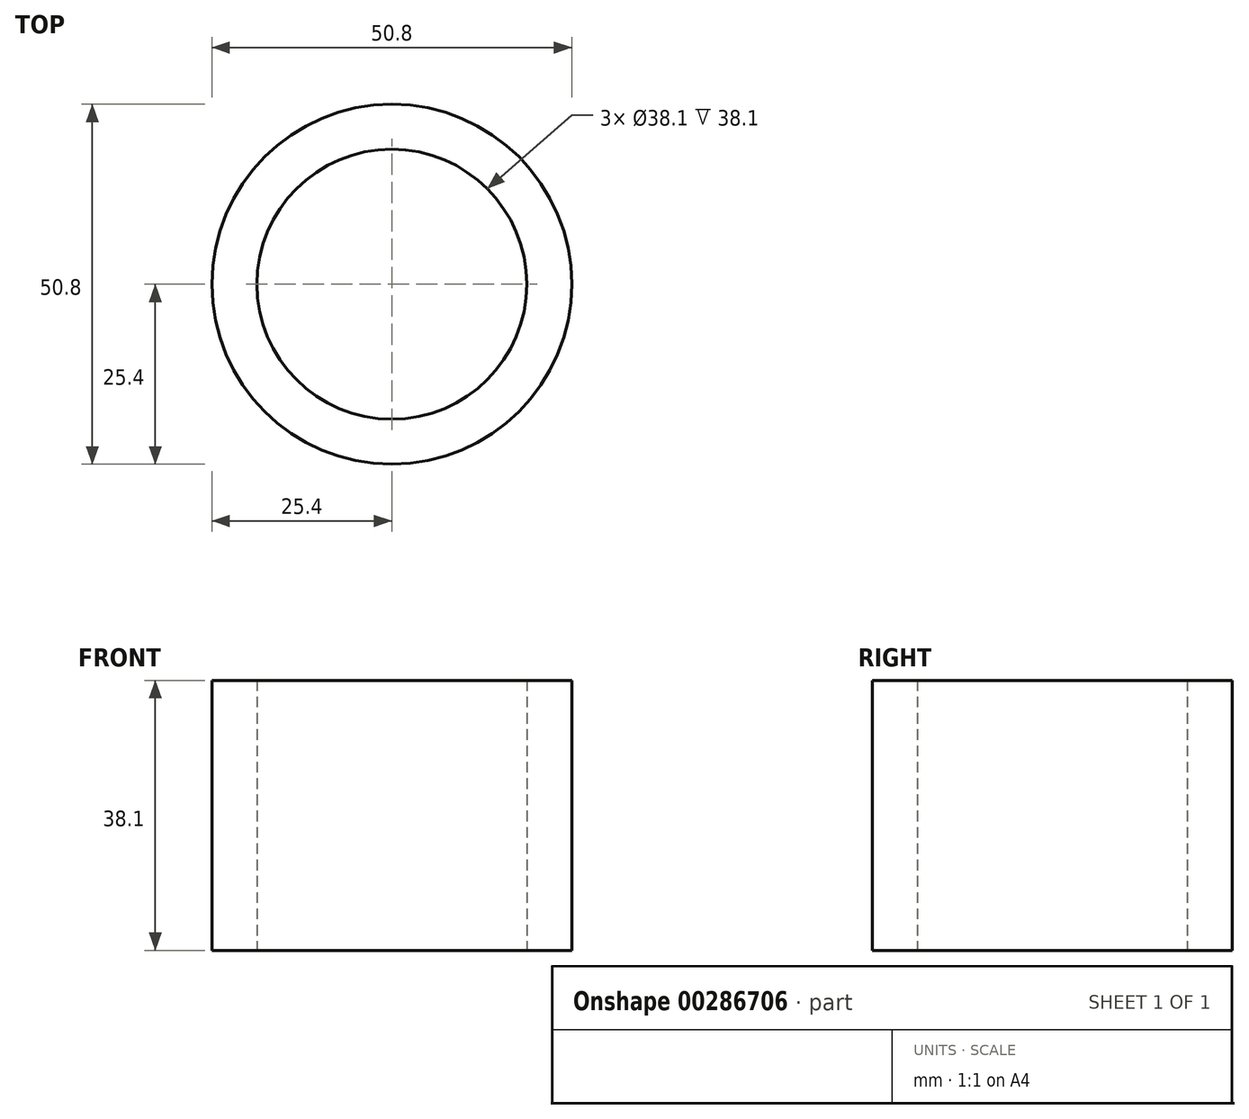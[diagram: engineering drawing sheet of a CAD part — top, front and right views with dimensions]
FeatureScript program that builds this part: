
annotation { "Feature Type Name" : "Feature", "Feature Type Description" : "" }
export const myFeature = defineFeature(function(context is Context, id is Id, definition is map)
    precondition{}
    {
        {
            var Q0;
            Q0=qCreatedBy(makeId("Top.planeOp"),FACE);
            var sketch = newSketch(context, id + "F0", { "sketchPlane" : qUnion([Q0])});
            skCircle(sketch, "E0", {"center": v(0, 0) * mm, "radius": 19.05 * mm});
            skCircle(sketch, "E1", {"center": v(0, 0) * mm, "radius": 25.4 * mm});
            skCircle(sketch, "E2", {"center": v(127, 0) * mm, "radius": 12.7 * mm});
            skLineSegment(sketch, "E3", {"start": v(2.54, 25.27) * mm, "end": v(128.27, 12.64) * mm});
            skLineSegment(sketch, "E4", {"start": v(2.54, -25.27) * mm, "end": v(128.27, -12.64) * mm});
            skLineSegment(sketch, "E5", {"start": v(38.1, 6.35) * mm, "end": v(88.9, 6.35) * mm});
            skLineSegment(sketch, "E6", {"start": v(38.1, -6.35) * mm, "end": v(88.9, -6.35) * mm});
            skArc(sketch, "E7", {"start": v(38.1, 6.35) * mm, "mid": v(31.75, 0) * mm, "end": v(38.1, -6.35) * mm});
            skArc(sketch, "E8", {"start": v(88.9, -6.35) * mm, "mid": v(95.25, 0) * mm, "end": v(88.9, 6.35) * mm});
            skCircle(sketch, "E9", {"center": v(127, 0) * mm, "radius": 6.35 * mm});
            skSolve(sketch);
        }
        {
            var Q0;
            Q0=makeQuery(id+"F0.imprint","IMPRINT",FACE,{"disambiguationData":[TD([[makeQuery(id+"F0.imprint","IMPRINT",EDGE,{"derivedFrom":sQuery(id+"F0.wireOp",EDGE,"E0")}),-1.0]])]});
            extrude(context, id + "F1", {"entities" : qUnion([Q0]), "depth" : 38.1 * mm});
        }
    });
